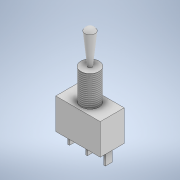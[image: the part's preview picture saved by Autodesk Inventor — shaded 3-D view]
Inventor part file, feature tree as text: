
AUTODESK INVENTOR PART (.ipt)
format: ipt  version: 2021 (Build 250183000, 183)  size: 173,056 bytes
history: native  units: mm
features: sketch x5, extrude x4, revolve x1, thread x1
ambient origin geometry x8: Origin, YZ Plane, XZ Plane, XY Plane, X Axis, Y Axis, Z Axis, Center Point
bodies: Solid1 (feature_tree)
feature tree (11):
  extrude  "Extrusion1"  Depth=9.0mm
  extrude  "Extrusion2"  Depth=4.5mm
  extrude  "Extrusion3"  Depth=0.5mm
  extrude  "Extrusion4"  Depth=0.5mm
  revolve  "Revolution1"  [1 undecoded]
  thread  "Thread1"  [1 undecoded]
  sketch  "Sketch1"  dims[d0=13.0mm d1=9.0mm]
  sketch  "Sketch2"  dims[d2=4.5mm d3=6.5mm]
  sketch  "Sketch3"  dims[d4=7.0mm d5=0.0mm d6=0.5mm]
  sketch  "Sketch4"  dims[d7=0.5mm d8=0.5mm]
  sketch  "Sketch5"  dims[d9=1.0mm d10=1.0mm d11=6.25mm d12=6.25mm d13=2.0mm d14=2.0mm d15=2.0mm d16=2.5mm d17=4.0mm d18=0.0mm d19=5.3mm d20=9.0mm d21=0.0mm d22=0.0mm d23=0.1mm d24=0.5mm d25=0.5mm d26=3.0mm d27=0.0mm d28=10.0mm d29=1.5mm d30=1.1mm d31=1.0mm d32=1.6mm d33=90.0deg d34=9.0mm d35=0.0mm]
note: 2 required parameter values undecoded (feature->parameter linkage not recoverable at this tier; creation-order binding heuristic only, values carry confidence <= 0.55)